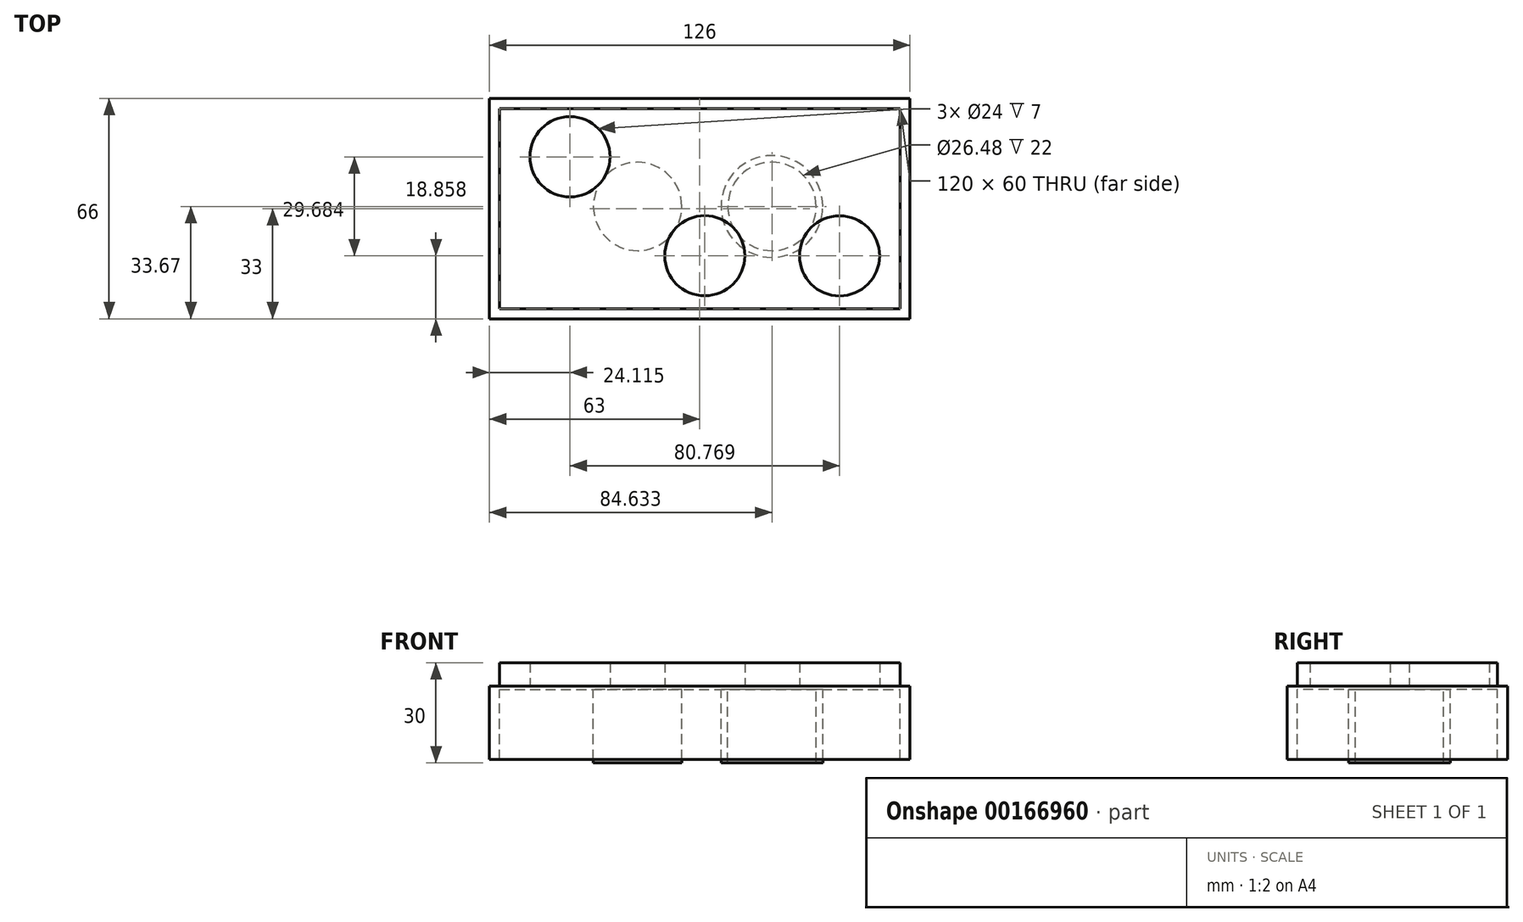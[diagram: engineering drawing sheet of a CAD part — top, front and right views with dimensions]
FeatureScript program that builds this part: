
annotation { "Feature Type Name" : "Feature", "Feature Type Description" : "" }
export const myFeature = defineFeature(function(context is Context, id is Id, definition is map)
    precondition{}
    {
        {
            var Q0;
            Q0=qCreatedBy(makeId("Top.planeOp"),FACE);
            var sketch = newSketch(context, id + "F0", { "sketchPlane" : qUnion([Q0])});
            skLineSegment(sketch, "E0.bottom", {"start": v(-64.5, 31.5) * mm, "end": v(61.5, 31.5) * mm});
            skLineSegment(sketch, "E0.top", {"start": v(-64.5, -34.5) * mm, "end": v(61.5, -34.5) * mm});
            skLineSegment(sketch, "E0.left", {"start": v(-64.5, 31.5) * mm, "end": v(-64.5, -34.5) * mm});
            skLineSegment(sketch, "E0.right", {"start": v(61.5, 31.5) * mm, "end": v(61.5, -34.5) * mm});
            skCircle(sketch, "E1.0", {"center": v(0, 14) * mm, "radius": 12 * mm});
            skCircle(sketch, "E2.MirrorC", {"center": v(0, -15.6) * mm, "radius": 12 * mm});
            skCircle(sketch, "E3.0", {"center": v(40.38, 14.04) * mm, "radius": 12 * mm});
            skCircle(sketch, "E4.MirrorC", {"center": v(-40.38, 14.04) * mm, "radius": 12 * mm});
            skCircle(sketch, "E5.MirrorC", {"center": v(-40.38, -15.64) * mm, "radius": 12 * mm});
            skCircle(sketch, "E6.MirrorC", {"center": v(40.38, -15.64) * mm, "radius": 12 * mm});
            skLineSegment(sketch, "E7.0", {"start": v(-61.5, 28.5) * mm, "end": v(58.5, 28.5) * mm});
            skLineSegment(sketch, "E7.1", {"start": v(-61.5, 28.5) * mm, "end": v(-61.5, -31.5) * mm});
            skLineSegment(sketch, "E7.2", {"start": v(-61.5, -31.5) * mm, "end": v(58.5, -31.5) * mm});
            skLineSegment(sketch, "E7.3", {"start": v(58.5, 28.5) * mm, "end": v(58.5, -31.5) * mm});
            skLineSegment(sketch, "E8", {"start": v(0, 0) * mm, "end": v(0, 28.5) * mm, "construction": true});
            skLineSegment(sketch, "E9", {"start": v(0, 14.25) * mm, "end": v(58.5, 14.25) * mm, "construction": true});
            skLineSegment(sketch, "E10", {"start": v(0, 0) * mm, "end": v(0, -31.5) * mm, "construction": true});
            skLineSegment(sketch, "E11", {"start": v(0, -15.75) * mm, "end": v(58.5, -15.75) * mm, "construction": true});
            skSolve(sketch);
        }
        {
            var Q0;
            Q0 = qSketchRegion(id + "F0", true);
            extrude(context, id + "F1", {"entities" : qUnion([Q0]), "oppositeDirection" : true, "depth" : 21 * mm});
        }
        {
            var Q0;
            Q0=makeQuery(id+"F0.imprint","IMPRINT",FACE,{"disambiguationData":[TD([[makeQuery(id+"F0.imprint","IMPRINT",EDGE,{"derivedFrom":sQuery(id+"F0.wireOp",EDGE,"E0.bottom")}),-1.0]])]});
            var sketch = newSketch(context, id + "F2", { "sketchPlane" : qUnion([Q0])});
            skLineSegment(sketch, "E12.0", {"start": v(61.5, 31.5) * mm, "end": v(61.5, -34.5) * mm});
            skLineSegment(sketch, "E12.1", {"start": v(-64.5, -34.5) * mm, "end": v(61.5, -34.5) * mm});
            skLineSegment(sketch, "E12.2", {"start": v(-64.5, 31.5) * mm, "end": v(-64.5, -34.5) * mm});
            skLineSegment(sketch, "E12.3", {"start": v(-64.5, 31.5) * mm, "end": v(61.5, 31.5) * mm});
            skSolve(sketch);
        }
        {
            var Q0;
            Q0 = qSketchRegion(id + "F2", true);
            extrude(context, id + "F3", {"entities" : qUnion([Q0]), "operationType" : NewBodyOperationType.ADD, "depth" : 1 * mm});
        }
        {
            var Q0;
            Q0=makeQuery(id+"F0.imprint","IMPRINT",FACE,{"disambiguationData":[TD([[makeQuery(id+"F0.imprint","IMPRINT",EDGE,{"derivedFrom":sQuery(id+"F0.wireOp",EDGE,"E4.MirrorC")}),-1.0]])]});
            var Q1;
            Q1=makeQuery(id+"F0.imprint","IMPRINT",FACE,{"disambiguationData":[TD([[makeQuery(id+"F0.imprint","IMPRINT",EDGE,{"derivedFrom":sQuery(id+"F0.wireOp",EDGE,"E1.0")}),1.0]])]});
            var Q2;
            Q2=makeQuery(id+"F0.imprint","IMPRINT",FACE,{"disambiguationData":[TD([[makeQuery(id+"F0.imprint","IMPRINT",EDGE,{"derivedFrom":sQuery(id+"F0.wireOp",EDGE,"E5.MirrorC")}),1.0]])]});
            var Q3;
            Q3=makeQuery(id+"F0.imprint","IMPRINT",FACE,{"disambiguationData":[TD([[makeQuery(id+"F0.imprint","IMPRINT",EDGE,{"derivedFrom":sQuery(id+"F0.wireOp",EDGE,"E2.MirrorC")}),-1.0]])]});
            var Q4;
            Q4=makeQuery(id+"F0.imprint","IMPRINT",FACE,{"disambiguationData":[TD([[makeQuery(id+"F0.imprint","IMPRINT",EDGE,{"derivedFrom":sQuery(id+"F0.wireOp",EDGE,"E6.MirrorC")}),-1.0]])]});
            var Q5;
            Q5=makeQuery(id+"F0.imprint","IMPRINT",FACE,{"disambiguationData":[TD([[makeQuery(id+"F0.imprint","IMPRINT",EDGE,{"derivedFrom":sQuery(id+"F0.wireOp",EDGE,"E3.0")}),1.0]])]});
            extrude(context, id + "F4", {"entities" : qUnion([Q0, Q1, Q2, Q3, Q4, Q5]), "operationType" : NewBodyOperationType.ADD, "depth" : 8 * mm});
        }
        {
            var Q0;
            Q0=makeQuery(id+"F0.imprint","IMPRINT",FACE,{"disambiguationData":[TD([[makeQuery(id+"F0.imprint","IMPRINT",EDGE,{"derivedFrom":sQuery(id+"F0.wireOp",EDGE,"E1.0")}),-1.0]])]});
            var sketch = newSketch(context, id + "F5", { "sketchPlane" : qUnion([Q0])});
            skLineSegment(sketch, "E13", {"start": v(12, 14.1) * mm, "end": v(28.27, 14.1) * mm, "construction": true});
            skLineSegment(sketch, "E14", {"start": v(20.13, 14.1) * mm, "end": v(20.13, -15.76) * mm, "construction": true});
            skCircle(sketch, "E15", {"center": v(20.13, -0.83) * mm, "radius": 13.24 * mm});
            skCircle(sketch, "E16.0", {"center": v(20.13, -0.83) * mm, "radius": 15.24 * mm});
            skLineSegment(sketch, "E17", {"start": v(0, -26.86) * mm, "end": v(0, 23.76) * mm, "construction": true});
            skCircle(sketch, "E18.MirrorC", {"center": v(-20.13, -0.83) * mm, "radius": 13.24 * mm});
            skCircle(sketch, "E19.MirrorC", {"center": v(-20.13, -0.83) * mm, "radius": 15.24 * mm});
            skSolve(sketch);
        }
        {
            var Q0;
            {var subQ0=sQuery(id+"F5.wireOp",EDGE,"E15");var subQ1=makeQuery(id+"F0.imprint","IMPRINT",EDGE,{"derivedFrom":sQuery(id+"F0.wireOp",EDGE,"E3.0")});var subQ2=makeQuery(id+"F5.imprint","INTERSECT",VERTEX,{"disambiguationData":[OD(0.0)],"derivedFrom":[subQ1,subQ0]});Q0=makeQuery(id+"F5.imprint","IMPRINT",FACE,{"disambiguationData":[TD([[makeQuery(id+"F5.imprint","IMPRINT",EDGE,{"disambiguationData":[TD([[subQ2,1.0]])],"derivedFrom":subQ0}),-1.0]])]});}
            var Q1;
            {var subQ0=sQuery(id+"F5.wireOp",EDGE,"E15");var subQ1=makeQuery(id+"F0.imprint","IMPRINT",EDGE,{"derivedFrom":sQuery(id+"F0.wireOp",EDGE,"E3.0")});var subQ2=makeQuery(id+"F5.imprint","INTERSECT",VERTEX,{"disambiguationData":[OD(0.0)],"derivedFrom":[subQ1,subQ0]});Q1=makeQuery(id+"F5.imprint","IMPRINT",FACE,{"disambiguationData":[TD([[makeQuery(id+"F5.imprint","IMPRINT",EDGE,{"disambiguationData":[TD([[subQ2,-1.0]])],"derivedFrom":subQ0}),-1.0]])]});}
            var Q2;
            {var subQ0=sQuery(id+"F5.wireOp",EDGE,"E15");var subQ1=makeQuery(id+"F0.imprint","IMPRINT",EDGE,{"derivedFrom":sQuery(id+"F0.wireOp",EDGE,"E1.0")});var subQ2=makeQuery(id+"F5.imprint","INTERSECT",VERTEX,{"disambiguationData":[OD(0.0)],"derivedFrom":[subQ1,subQ0]});Q2=makeQuery(id+"F5.imprint","IMPRINT",FACE,{"disambiguationData":[TD([[makeQuery(id+"F5.imprint","IMPRINT",EDGE,{"disambiguationData":[TD([[subQ2,-1.0]])],"derivedFrom":subQ0}),-1.0]])]});}
            var Q3;
            {var subQ0=sQuery(id+"F5.wireOp",EDGE,"E15");var subQ1=makeQuery(id+"F0.imprint","IMPRINT",EDGE,{"derivedFrom":sQuery(id+"F0.wireOp",EDGE,"E1.0")});var subQ2=makeQuery(id+"F5.imprint","INTERSECT",VERTEX,{"disambiguationData":[OD(1.0)],"derivedFrom":[subQ1,subQ0]});Q3=makeQuery(id+"F5.imprint","IMPRINT",FACE,{"disambiguationData":[TD([[makeQuery(id+"F5.imprint","IMPRINT",EDGE,{"disambiguationData":[TD([[subQ2,-1.0]])],"derivedFrom":subQ0}),-1.0]])]});}
            var Q4;
            {var subQ0=sQuery(id+"F5.wireOp",EDGE,"E15");var subQ1=makeQuery(id+"F0.imprint","IMPRINT",EDGE,{"derivedFrom":sQuery(id+"F0.wireOp",EDGE,"E2.MirrorC")});var subQ2=makeQuery(id+"F5.imprint","INTERSECT",VERTEX,{"disambiguationData":[OD(0.0)],"derivedFrom":[subQ1,subQ0]});Q4=makeQuery(id+"F5.imprint","IMPRINT",FACE,{"disambiguationData":[TD([[makeQuery(id+"F5.imprint","IMPRINT",EDGE,{"disambiguationData":[TD([[subQ2,-1.0]])],"derivedFrom":subQ0}),-1.0]])]});}
            var Q5;
            {var subQ0=sQuery(id+"F5.wireOp",EDGE,"E15");var subQ1=makeQuery(id+"F0.imprint","IMPRINT",EDGE,{"derivedFrom":sQuery(id+"F0.wireOp",EDGE,"E2.MirrorC")});var subQ2=makeQuery(id+"F5.imprint","INTERSECT",VERTEX,{"disambiguationData":[OD(1.0)],"derivedFrom":[subQ1,subQ0]});Q5=makeQuery(id+"F5.imprint","IMPRINT",FACE,{"disambiguationData":[TD([[makeQuery(id+"F5.imprint","IMPRINT",EDGE,{"disambiguationData":[TD([[subQ2,-1.0]])],"derivedFrom":subQ0}),-1.0]])]});}
            var Q6;
            {var subQ0=sQuery(id+"F5.wireOp",EDGE,"E15");var subQ1=makeQuery(id+"F0.imprint","IMPRINT",EDGE,{"derivedFrom":sQuery(id+"F0.wireOp",EDGE,"E6.MirrorC")});var subQ2=makeQuery(id+"F5.imprint","INTERSECT",VERTEX,{"disambiguationData":[OD(0.0)],"derivedFrom":[subQ1,subQ0]});Q6=makeQuery(id+"F5.imprint","IMPRINT",FACE,{"disambiguationData":[TD([[makeQuery(id+"F5.imprint","IMPRINT",EDGE,{"disambiguationData":[TD([[subQ2,-1.0]])],"derivedFrom":subQ0}),-1.0]])]});}
            var Q7;
            {var subQ0=sQuery(id+"F5.wireOp",EDGE,"E15");var subQ1=makeQuery(id+"F0.imprint","IMPRINT",EDGE,{"derivedFrom":sQuery(id+"F0.wireOp",EDGE,"E3.0")});var subQ2=makeQuery(id+"F5.imprint","INTERSECT",VERTEX,{"disambiguationData":[OD(1.0)],"derivedFrom":[subQ1,subQ0]});Q7=makeQuery(id+"F5.imprint","IMPRINT",FACE,{"disambiguationData":[TD([[makeQuery(id+"F5.imprint","IMPRINT",EDGE,{"disambiguationData":[TD([[subQ2,1.0]])],"derivedFrom":subQ0}),-1.0]])]});}
            var Q8;
            {var subQ0=sQuery(id+"F5.wireOp",EDGE,"E18.MirrorC");var subQ1=makeQuery(id+"F0.imprint","IMPRINT",EDGE,{"derivedFrom":sQuery(id+"F0.wireOp",EDGE,"E4.MirrorC")});var subQ2=makeQuery(id+"F5.imprint","INTERSECT",VERTEX,{"disambiguationData":[OD(0.0)],"derivedFrom":[subQ1,subQ0]});Q8=makeQuery(id+"F5.imprint","IMPRINT",FACE,{"disambiguationData":[TD([[makeQuery(id+"F5.imprint","IMPRINT",EDGE,{"disambiguationData":[TD([[subQ2,1.0]])],"derivedFrom":subQ0}),1.0]])]});}
            var Q9;
            {var subQ0=sQuery(id+"F5.wireOp",EDGE,"E18.MirrorC");var subQ1=makeQuery(id+"F0.imprint","IMPRINT",EDGE,{"derivedFrom":sQuery(id+"F0.wireOp",EDGE,"E4.MirrorC")});var subQ2=makeQuery(id+"F5.imprint","INTERSECT",VERTEX,{"disambiguationData":[OD(0.0)],"derivedFrom":[subQ1,subQ0]});Q9=makeQuery(id+"F5.imprint","IMPRINT",FACE,{"disambiguationData":[TD([[makeQuery(id+"F5.imprint","IMPRINT",EDGE,{"disambiguationData":[TD([[subQ2,-1.0]])],"derivedFrom":subQ0}),1.0]])]});}
            var Q10;
            {var subQ0=sQuery(id+"F5.wireOp",EDGE,"E18.MirrorC");var subQ1=makeQuery(id+"F0.imprint","IMPRINT",EDGE,{"derivedFrom":sQuery(id+"F0.wireOp",EDGE,"E1.0")});var subQ2=makeQuery(id+"F5.imprint","INTERSECT",VERTEX,{"disambiguationData":[OD(0.0)],"derivedFrom":[subQ1,subQ0]});Q10=makeQuery(id+"F5.imprint","IMPRINT",FACE,{"disambiguationData":[TD([[makeQuery(id+"F5.imprint","IMPRINT",EDGE,{"disambiguationData":[TD([[subQ2,-1.0]])],"derivedFrom":subQ0}),1.0]])]});}
            var Q11;
            {var subQ0=sQuery(id+"F5.wireOp",EDGE,"E18.MirrorC");var subQ1=makeQuery(id+"F0.imprint","IMPRINT",EDGE,{"derivedFrom":sQuery(id+"F0.wireOp",EDGE,"E1.0")});var subQ2=makeQuery(id+"F5.imprint","INTERSECT",VERTEX,{"disambiguationData":[OD(1.0)],"derivedFrom":[subQ1,subQ0]});Q11=makeQuery(id+"F5.imprint","IMPRINT",FACE,{"disambiguationData":[TD([[makeQuery(id+"F5.imprint","IMPRINT",EDGE,{"disambiguationData":[TD([[subQ2,-1.0]])],"derivedFrom":subQ0}),1.0]])]});}
            var Q12;
            {var subQ0=sQuery(id+"F5.wireOp",EDGE,"E18.MirrorC");var subQ1=makeQuery(id+"F0.imprint","IMPRINT",EDGE,{"derivedFrom":sQuery(id+"F0.wireOp",EDGE,"E2.MirrorC")});var subQ2=makeQuery(id+"F5.imprint","INTERSECT",VERTEX,{"disambiguationData":[OD(0.0)],"derivedFrom":[subQ1,subQ0]});Q12=makeQuery(id+"F5.imprint","IMPRINT",FACE,{"disambiguationData":[TD([[makeQuery(id+"F5.imprint","IMPRINT",EDGE,{"disambiguationData":[TD([[subQ2,-1.0]])],"derivedFrom":subQ0}),1.0]])]});}
            var Q13;
            {var subQ0=sQuery(id+"F5.wireOp",EDGE,"E18.MirrorC");var subQ1=makeQuery(id+"F0.imprint","IMPRINT",EDGE,{"derivedFrom":sQuery(id+"F0.wireOp",EDGE,"E2.MirrorC")});var subQ2=makeQuery(id+"F5.imprint","INTERSECT",VERTEX,{"disambiguationData":[OD(1.0)],"derivedFrom":[subQ1,subQ0]});Q13=makeQuery(id+"F5.imprint","IMPRINT",FACE,{"disambiguationData":[TD([[makeQuery(id+"F5.imprint","IMPRINT",EDGE,{"disambiguationData":[TD([[subQ2,-1.0]])],"derivedFrom":subQ0}),1.0]])]});}
            var Q14;
            {var subQ0=sQuery(id+"F5.wireOp",EDGE,"E18.MirrorC");var subQ1=makeQuery(id+"F0.imprint","IMPRINT",EDGE,{"derivedFrom":sQuery(id+"F0.wireOp",EDGE,"E5.MirrorC")});var subQ2=makeQuery(id+"F5.imprint","INTERSECT",VERTEX,{"disambiguationData":[OD(0.0)],"derivedFrom":[subQ1,subQ0]});Q14=makeQuery(id+"F5.imprint","IMPRINT",FACE,{"disambiguationData":[TD([[makeQuery(id+"F5.imprint","IMPRINT",EDGE,{"disambiguationData":[TD([[subQ2,-1.0]])],"derivedFrom":subQ0}),1.0]])]});}
            var Q15;
            {var subQ0=sQuery(id+"F5.wireOp",EDGE,"E18.MirrorC");var subQ1=makeQuery(id+"F0.imprint","IMPRINT",EDGE,{"derivedFrom":sQuery(id+"F0.wireOp",EDGE,"E4.MirrorC")});var subQ2=makeQuery(id+"F5.imprint","INTERSECT",VERTEX,{"disambiguationData":[OD(1.0)],"derivedFrom":[subQ1,subQ0]});Q15=makeQuery(id+"F5.imprint","IMPRINT",FACE,{"disambiguationData":[TD([[makeQuery(id+"F5.imprint","IMPRINT",EDGE,{"disambiguationData":[TD([[subQ2,1.0]])],"derivedFrom":subQ0}),1.0]])]});}
            extrude(context, id + "F6", {"entities" : qUnion([Q0, Q1, Q2, Q3, Q4, Q5, Q6, Q7, Q8, Q9, Q10, Q11, Q12, Q13, Q14, Q15]), "operationType" : NewBodyOperationType.ADD, "oppositeDirection" : true, "depth" : 22 * mm});
        }
    });
